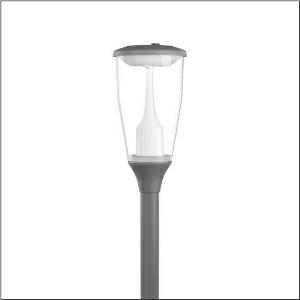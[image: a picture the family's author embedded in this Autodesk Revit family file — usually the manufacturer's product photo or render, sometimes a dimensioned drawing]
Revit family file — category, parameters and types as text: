
# Revit family: dl_11_iq___st1_2a_5xa5575ev14hp00022_13c9
name_source: partatom
category: Lighting Fixtures
units: mm (PartAtom-declared; Revit-internal decimal feet)

## family parameters
Cut with Voids When Loaded = No
Host = Face
Light Source = No
Part Type = Normal
Room Calculation Point = No
Round Connector Dimension = Use Diameter
Shared = No

## types (1)
- --- (1 x LED, 4790 lm, 33.5 W, 3000K)
    Apparent Load = 34 VA
    CIE Flux Codes = 23 60 93 95 100
    Color Rendering = 70
    Color Temperature = 3000K
    Default Elevation = 1800 mm
    Description = DL 11 iQ, mast luminaire, Module 540 iQ-SR, primary light control with 3 zone facetted reflector, of plastic, silver coated, highly specular, structured, primary optical cover: cover, of PMMA, transparent, light distribution: ST1.2a, light emission: direct distribution, primary light characteristic: asymmetric, installation type: post-top, LED, High Power LED, rated luminous flux: 4.790lm, luminous efficacy: 143lm/W, light colour: 730, colour temperature: 3000K, control gear: iQ-Street Remote, D4i with power reduction, control: pre-setting: logarithmic dimming characteristic, Street-Remote, Auto-Match, Temp-Guard, Lumen-Switch, Night-Set, Smart-Wire, Light-Fading, Desk-Remote (wireless, voltage-free reading and setting of iQ features in the workshop via application-optimized NFC function/RFID function), optimised constant luminous flux control (CLO 2.0), mains connection: 220..240V, AC, 50/60Hz, connection cable pre-assembled, cable length: 5,5m, start of lifetime: 34W, end of service life: 36W, reduction: 15W, luminaire housing, upper part, of diecast aluminium, coated, Siteco® metallic grey (DB 702S), spigot size: 76mm (post-top), mounting height: 3..5m, post-top mast mounting element, of diecast aluminium, coated, Siteco® metallic grey (DB 702S), Module 540 iQ-SR, traffic white (RAL 9016), equipment: Power, Smart Interface above, protection rating (complete): IP66, insulation class (complete): insulation class II (safety insulation), certification: CE, ENEC, ENEC+, VDE, impact resistance: IK07, packaging unit: 1 piece

Light Distribution: ST1.2a
    Height = 665 mm
    Lamp = 1 x LED
    Lamp Light Flux = 4790 lm
    Lamp Power = 33.5 W
    Lamp count = 1
    Length = 334 mm
    Luminous efficacy = 143 lm/W
    Manufacturer = Siteco
    ModVariant = No
    Model = 5XA5575EV14HP00022
    Number of Poles = 1
    OnlyDefault = Yes
    Power Factor = 1
    Product Name = DL 11 iQ | ST1.2a
    Product group = mast luminaire | pylon top
    ProductGroupID = 6100
    Protection Class = Protection class II
    Protection Degree = IP 66
    RLX_Detail_Level = 1
    RLX_Emergency_Light_Flux = 0 lm
    RLX_Emergency_Type = 0
    RLX_Emergency_Type_DB = No
    RlxData = <blob elided: 161277 chars, md5=e0bc52b4>
    Socket = socket
    Standby Power = 0 W
    System Light Flux = 4790 lm
    System Power = 34 W
    Type Comments = factory setting: luminous flux: 100 % | dim-lin: 254 | 695 mA
    Type Image = l_1337541.jpg
    URL = http://relux.com
    VarID = @adj_033854
    Voltage = 0 V
    Weight = 0.00 kg
    Width = 0 mm  [stored 0 ft]

note: [stored X ft] marks values corroborated as IEEE doubles in the binary element streams (Revit-internal decimal feet)

## geometry (parser evidence)
native form markers: Blend x4, Sweep x13
no freeform markers — native parametric forms only
